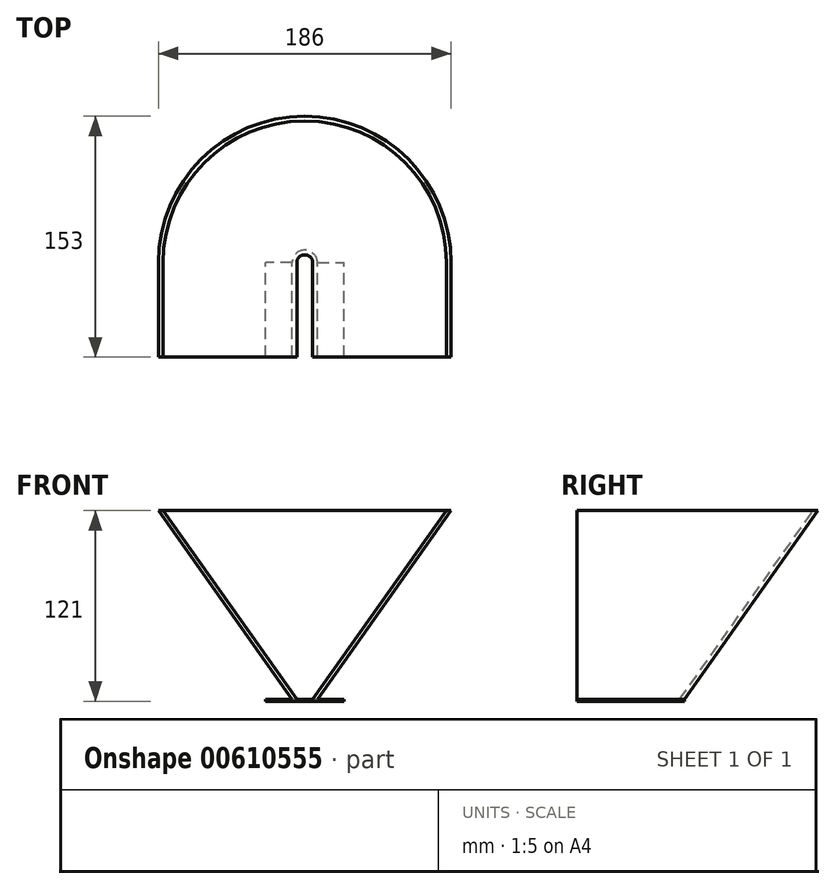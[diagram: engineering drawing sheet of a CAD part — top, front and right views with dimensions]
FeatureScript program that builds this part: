
annotation { "Feature Type Name" : "Feature", "Feature Type Description" : "" }
export const myFeature = defineFeature(function(context is Context, id is Id, definition is map)
    precondition{}
    {
        {
            var Q0;
            Q0=qCreatedBy(makeId("Top.planeOp"),FACE);
            var sketch = newSketch(context, id + "F0", { "sketchPlane" : qUnion([Q0])});
            skLineSegment(sketch, "E0", {"start": v(5, 0) * mm, "end": v(5, 60) * mm});
            skLineSegment(sketch, "E1", {"start": v(-5, 0) * mm, "end": v(-5, 60) * mm});
            skArc(sketch, "E2", {"start": v(-5, 60) * mm, "mid": v(0, 65) * mm, "end": v(5, 60) * mm});
            skLineSegment(sketch, "E3", {"start": v(5, 0) * mm, "end": v(8, 0) * mm});
            skLineSegment(sketch, "E4", {"start": v(8, 0) * mm, "end": v(8, 60) * mm});
            skLineSegment(sketch, "E5", {"start": v(-5, 0) * mm, "end": v(-8, 0) * mm});
            skLineSegment(sketch, "E6", {"start": v(-8, 0) * mm, "end": v(-8, 60) * mm});
            skArc(sketch, "E7", {"start": v(-8, 60) * mm, "mid": v(0, 68) * mm, "end": v(8, 60) * mm});
            skSolve(sketch);
        }
        {
            var Q0;
            Q0=qCreatedBy(makeId("Top.planeOp"),FACE);
            cPlane(context, id + "F1", {"entities" : qUnion([Q0]), "cplaneType" : CPlaneType.OFFSET, "offset" : 120 * mm, "width" : 150 * mm, "height" : 150 * mm});
        }
        {
            var Q0;
            Q0=qCreatedBy(id+"F1.planeOp",FACE);
            var sketch = newSketch(context, id + "F2", { "sketchPlane" : qUnion([Q0])});
            skLineSegment(sketch, "E8", {"start": v(-90, 60) * mm, "end": v(-90, 0) * mm});
            skLineSegment(sketch, "E9", {"start": v(-90, 0) * mm, "end": v(-93, 0) * mm});
            skLineSegment(sketch, "E10", {"start": v(-93, 0) * mm, "end": v(-93, 60) * mm});
            skLineSegment(sketch, "E11", {"start": v(90, 60) * mm, "end": v(90, 0) * mm});
            skLineSegment(sketch, "E12", {"start": v(90, 0) * mm, "end": v(93, 0) * mm});
            skLineSegment(sketch, "E13", {"start": v(93, 0) * mm, "end": v(93, 60) * mm});
            skArc(sketch, "E14", {"start": v(-90, 60) * mm, "mid": v(0, 150) * mm, "end": v(90, 60) * mm});
            skArc(sketch, "E15", {"start": v(-93, 60) * mm, "mid": v(0, 153) * mm, "end": v(93, 60) * mm});
            skSolve(sketch);
        }
        {
            var Q0;
            Q0=makeQuery(id+"F0.imprint","IMPRINT",FACE,{"disambiguationData":[TD([[makeQuery(id+"F0.imprint","IMPRINT",EDGE,{"derivedFrom":sQuery(id+"F0.wireOp",EDGE,"E0")}),-1.0]])]});
            var Q1;
            Q1=makeQuery(id+"F2.imprint","IMPRINT",FACE,{"disambiguationData":[TD([[makeQuery(id+"F2.imprint","IMPRINT",EDGE,{"derivedFrom":sQuery(id+"F2.wireOp",EDGE,"E8")}),-1.0]])]});
            loft(context, id + "F3", {"sheetProfilesArray" : [{ "sheetProfileEntities" : qUnion([Q0]) }, { "sheetProfileEntities" : qUnion([Q1]) }]});
        }
        {
            var Q0;
            Q0=makeQuery(id+"F3.opLoft","CAP_FACE",FACE,{"disambiguationData":[OSD([makeQuery(id+"F0.imprint","IMPRINT",FACE,{"disambiguationData":[TD([[makeQuery(id+"F0.imprint","IMPRINT",EDGE,{"derivedFrom":sQuery(id+"F0.wireOp",EDGE,"E0")}),-1.0]])]})])],"isStart":true});
            var sketch = newSketch(context, id + "F4", { "sketchPlane" : qUnion([Q0])});
            skLineSegment(sketch, "E16.bottom", {"start": v(-5, 0) * mm, "end": v(-25, 0) * mm});
            skLineSegment(sketch, "E16.top", {"start": v(-5, -60) * mm, "end": v(-25, -60) * mm});
            skLineSegment(sketch, "E16.left", {"start": v(-5, 0) * mm, "end": v(-5, -60) * mm});
            skLineSegment(sketch, "E16.right", {"start": v(-25, 0) * mm, "end": v(-25, -60) * mm});
            skLineSegment(sketch, "E17.MirrorCS", {"start": v(5, 0) * mm, "end": v(5, -60) * mm});
            skLineSegment(sketch, "E18.MirrorCS", {"start": v(25, 0) * mm, "end": v(25, -60) * mm});
            skLineSegment(sketch, "E19.MirrorCS", {"start": v(5, -60) * mm, "end": v(25, -60) * mm});
            skLineSegment(sketch, "E20.MirrorCS", {"start": v(5, 0) * mm, "end": v(25, 0) * mm});
            skSolve(sketch);
        }
        {
            var Q0;
            {var subQ0=sQuery(id+"F0.wireOp",EDGE,"E2");var subQ1=sQuery(id+"F0.wireOp",EDGE,"E1");var subQ2=sQuery(id+"F0.wireOp",EDGE,"E0");var subQ3=makeQuery(id+"F3.opLoft","MID_CAP_EDGE",EDGE,{"disambiguationData":[OSD([subQ2,subQ1,subQ0])],"capPos":0.0});Q0=makeQuery(id+"F4.imprint","IMPRINT",FACE,{"disambiguationData":[TD([[makeQuery(id+"F4.imprint","IMPRINT",EDGE,{"derivedFrom":subQ3}),-1.0]])]});}
            var Q1;
            {var subQ3=sQuery(id+"F4.wireOp",EDGE,"E16.right");Q1=makeQuery(id+"F4.imprint","IMPRINT",FACE,{"disambiguationData":[TD([[makeQuery(id+"F4.imprint","IMPRINT",EDGE,{"derivedFrom":subQ3}),1.0]])]});}
            var Q2;
            {var subQ0=sQuery(id+"F4.wireOp",EDGE,"E18.MirrorCS");Q2=makeQuery(id+"F4.imprint","IMPRINT",FACE,{"disambiguationData":[TD([[makeQuery(id+"F4.imprint","IMPRINT",EDGE,{"derivedFrom":subQ0}),-1.0]])]});}
            var Q3;
            {var subQ0=sQuery(id+"F4.wireOp",EDGE,"E17.MirrorCS");Q3=makeQuery(id+"F4.imprint","IMPRINT",FACE,{"disambiguationData":[TD([[makeQuery(id+"F4.imprint","IMPRINT",EDGE,{"derivedFrom":subQ0}),-1.0]])]});}
            var Q4;
            {var subQ0=sQuery(id+"F4.wireOp",EDGE,"E16.left");Q4=makeQuery(id+"F4.imprint","IMPRINT",FACE,{"disambiguationData":[TD([[makeQuery(id+"F4.imprint","IMPRINT",EDGE,{"derivedFrom":subQ0}),-1.0]])]});}
            extrude(context, id + "F5", {"entities" : qUnion([Q0, Q1, Q2, Q3, Q4]), "operationType" : NewBodyOperationType.ADD, "depth" : 1 * mm, "offsetDistance" : 25 * mm});
        }
    });
